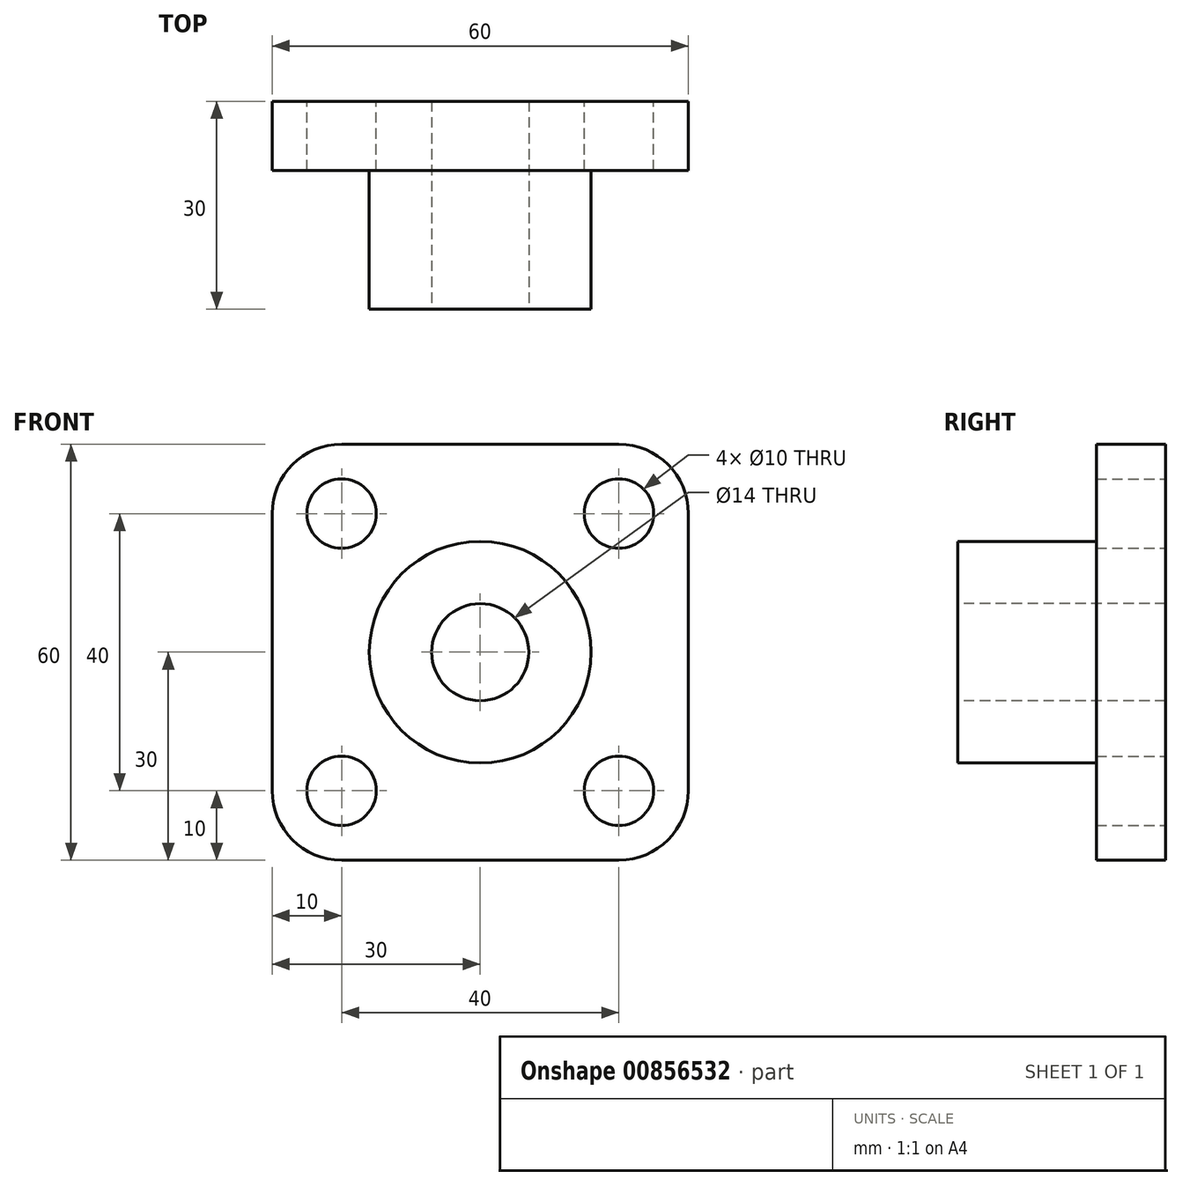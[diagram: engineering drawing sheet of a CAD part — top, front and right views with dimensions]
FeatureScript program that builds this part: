
annotation { "Feature Type Name" : "Feature", "Feature Type Description" : "" }
export const myFeature = defineFeature(function(context is Context, id is Id, definition is map)
    precondition{}
    {
        {
            var Q0;
            Q0=qCreatedBy(makeId("Front.planeOp"),FACE);
            var sketch = newSketch(context, id + "F0", { "sketchPlane" : qUnion([Q0])});
            skCircle(sketch, "E0", {"center": v(0, 0) * mm, "radius": 16 * mm});
            skLineSegment(sketch, "E1", {"start": v(0, 0) * mm, "end": v(-20, 0) * mm});
            skLineSegment(sketch, "E2", {"start": v(0, 0) * mm, "end": v(20, 0) * mm});
            skLineSegment(sketch, "E3", {"start": v(-20, 0) * mm, "end": v(-20, 20) * mm});
            skLineSegment(sketch, "E4", {"start": v(-20, 0) * mm, "end": v(-20, -20) * mm});
            skLineSegment(sketch, "E5", {"start": v(20, 0) * mm, "end": v(20, -20) * mm});
            skLineSegment(sketch, "E6", {"start": v(20, 0) * mm, "end": v(20, 20) * mm});
            skCircle(sketch, "E7", {"center": v(-20, 20) * mm, "radius": 5 * mm});
            skCircle(sketch, "E8", {"center": v(20, 20) * mm, "radius": 5 * mm});
            skCircle(sketch, "E9", {"center": v(-20, -20) * mm, "radius": 5 * mm});
            skCircle(sketch, "E10", {"center": v(20, -20) * mm, "radius": 5 * mm});
            skCircle(sketch, "E11", {"center": v(-20, 20) * mm, "radius": 10 * mm});
            skCircle(sketch, "E12", {"center": v(20, 20) * mm, "radius": 10 * mm});
            skCircle(sketch, "E13", {"center": v(-20, -20) * mm, "radius": 10 * mm});
            skCircle(sketch, "E14", {"center": v(20, -20) * mm, "radius": 10 * mm});
            skLineSegment(sketch, "E15", {"start": v(-20, -30) * mm, "end": v(20, -30) * mm});
            skLineSegment(sketch, "E16", {"start": v(30, 20) * mm, "end": v(30, -20) * mm});
            skLineSegment(sketch, "E17.trimOffspring", {"start": v(-20, 30) * mm, "end": v(20, 30) * mm});
            skLineSegment(sketch, "E18.trimOffspring", {"start": v(-30, 20) * mm, "end": v(-30, -20) * mm});
            skSolve(sketch);
        }
        {
            var Q0;
            {var subQ5=sQuery(id+"F0.wireOp",EDGE,"E17.trimOffspring");Q0=makeQuery(id+"F0.imprint","IMPRINT",FACE,{"disambiguationData":[TD([[makeQuery(id+"F0.imprint","IMPRINT",EDGE,{"derivedFrom":subQ5}),-1.0]])]});}
            var Q1;
            {var subQ13=sQuery(id+"F0.wireOp",EDGE,"E15");Q1=makeQuery(id+"F0.imprint","IMPRINT",FACE,{"disambiguationData":[TD([[makeQuery(id+"F0.imprint","IMPRINT",EDGE,{"derivedFrom":subQ13}),1.0]])]});}
            var Q2;
            {var subQ0=sQuery(id+"F0.wireOp",EDGE,"E16");Q2=makeQuery(id+"F0.imprint","IMPRINT",FACE,{"disambiguationData":[TD([[makeQuery(id+"F0.imprint","IMPRINT",EDGE,{"derivedFrom":subQ0}),-1.0]])]});}
            var Q3;
            Q3=makeQuery(id+"F0.imprint","IMPRINT",FACE,{"disambiguationData":[TD([[makeQuery(id+"F0.imprint","IMPRINT",EDGE,{"derivedFrom":sQuery(id+"F0.wireOp",EDGE,"E8")}),-1.0]])]});
            var Q4;
            Q4=makeQuery(id+"F0.imprint","IMPRINT",FACE,{"disambiguationData":[TD([[makeQuery(id+"F0.imprint","IMPRINT",EDGE,{"derivedFrom":sQuery(id+"F0.wireOp",EDGE,"E7")}),-1.0]])]});
            var Q5;
            {var subQ0=sQuery(id+"F0.wireOp",EDGE,"E18.trimOffspring");Q5=makeQuery(id+"F0.imprint","IMPRINT",FACE,{"disambiguationData":[TD([[makeQuery(id+"F0.imprint","IMPRINT",EDGE,{"derivedFrom":subQ0}),1.0]])]});}
            var Q6;
            Q6=makeQuery(id+"F0.imprint","IMPRINT",FACE,{"disambiguationData":[TD([[makeQuery(id+"F0.imprint","IMPRINT",EDGE,{"derivedFrom":sQuery(id+"F0.wireOp",EDGE,"E9")}),-1.0]])]});
            var Q7;
            Q7=makeQuery(id+"F0.imprint","IMPRINT",FACE,{"disambiguationData":[TD([[makeQuery(id+"F0.imprint","IMPRINT",EDGE,{"derivedFrom":sQuery(id+"F0.wireOp",EDGE,"E10")}),-1.0]])]});
            var Q8;
            {var subQ0=sQuery(id+"F0.wireOp",EDGE,"E1");var subQ1=sQuery(id+"F0.wireOp",EDGE,"E0");var subQ2=makeQuery(id+"F0.imprint","INTERSECT",VERTEX,{"derivedFrom":[subQ1,subQ0]});Q8=makeQuery(id+"F0.imprint","IMPRINT",FACE,{"disambiguationData":[TD([[makeQuery(id+"F0.imprint","IMPRINT",EDGE,{"disambiguationData":[TD([[subQ2,1.0]])],"derivedFrom":subQ1}),1.0]])]});}
            var Q9;
            {var subQ0=sQuery(id+"F0.wireOp",EDGE,"E1");var subQ1=sQuery(id+"F0.wireOp",EDGE,"E0");var subQ2=makeQuery(id+"F0.imprint","INTERSECT",VERTEX,{"derivedFrom":[subQ1,subQ0]});Q9=makeQuery(id+"F0.imprint","IMPRINT",FACE,{"disambiguationData":[TD([[makeQuery(id+"F0.imprint","IMPRINT",EDGE,{"disambiguationData":[TD([[subQ2,-1.0]])],"derivedFrom":subQ1}),1.0]])]});}
            extrude(context, id + "F1", {"entities" : qUnion([Q0, Q1, Q2, Q3, Q4, Q5, Q6, Q7, Q8, Q9]), "depth" : 10 * mm, "offsetDistance" : 25 * mm});
        }
        {
            var Q0;
            Q0=makeQuery(id+"F1.opExtrude","CAP_FACE",FACE,{"disambiguationData":[OSD([sQuery(id+"F0.wireOp",EDGE,"E0"),sQuery(id+"F0.wireOp",EDGE,"E7"),sQuery(id+"F0.wireOp",EDGE,"E8"),sQuery(id+"F0.wireOp",EDGE,"E9"),sQuery(id+"F0.wireOp",EDGE,"E10"),sQuery(id+"F0.wireOp",EDGE,"E11"),sQuery(id+"F0.wireOp",EDGE,"E12"),sQuery(id+"F0.wireOp",EDGE,"E13"),sQuery(id+"F0.wireOp",EDGE,"E14"),sQuery(id+"F0.wireOp",EDGE,"E15"),sQuery(id+"F0.wireOp",EDGE,"E16"),sQuery(id+"F0.wireOp",EDGE,"E17.trimOffspring"),sQuery(id+"F0.wireOp",EDGE,"E18.trimOffspring")])],"isStart":false});
            var sketch = newSketch(context, id + "F2", { "sketchPlane" : qUnion([Q0])});
            skCircle(sketch, "E19", {"center": v(0, 0) * mm, "radius": 16 * mm});
            skSolve(sketch);
        }
        {
            var Q0;
            Q0=makeQuery(id+"F2.imprint","IMPRINT",FACE,{"disambiguationData":[TD([[makeQuery(id+"F2.imprint","IMPRINT",EDGE,{"derivedFrom":sQuery(id+"F2.wireOp",EDGE,"E19")}),1.0]])]});
            extrude(context, id + "F3", {"entities" : qUnion([Q0]), "operationType" : NewBodyOperationType.ADD, "depth" : 20 * mm, "offsetDistance" : 25 * mm});
        }
        {
            var Q0;
            Q0=makeQuery(id+"F3.opExtrude","CAP_FACE",FACE,{"disambiguationData":[OSD([sQuery(id+"F2.wireOp",EDGE,"E19")])],"isStart":false});
            var sketch = newSketch(context, id + "F4", { "sketchPlane" : qUnion([Q0])});
            skPoint(sketch, "E20", {"position": v(0, 0) * mm});
            skSolve(sketch);
        }
        {
            var Q0;
            Q0=sQuery(id+"F4.wireOp",VERTEX,"E20");
            var Q1;
            Q1=makeQuery(id+"F1.opExtrude","SWEPT_BODY",BODY,{"disambiguationData":[OSD([sQuery(id+"F0.wireOp",EDGE,"E7"),sQuery(id+"F0.wireOp",EDGE,"E8"),sQuery(id+"F0.wireOp",EDGE,"E9"),sQuery(id+"F0.wireOp",EDGE,"E10"),sQuery(id+"F0.wireOp",EDGE,"E11"),sQuery(id+"F0.wireOp",EDGE,"E12"),sQuery(id+"F0.wireOp",EDGE,"E13"),sQuery(id+"F0.wireOp",EDGE,"E14"),sQuery(id+"F0.wireOp",EDGE,"E15"),sQuery(id+"F0.wireOp",EDGE,"E16"),sQuery(id+"F0.wireOp",EDGE,"E17.trimOffspring"),sQuery(id+"F0.wireOp",EDGE,"E18.trimOffspring")])]});
            hole(context, id + "F5", {"style" : HoleStyle.SIMPLE, "endStyle" : HoleEndStyle.THROUGH, "standardTappedOrClearance" : lookupTablePath({ "standard" : "ISO", "engagement" : "75%", "pitch" : "2 mm", "size" : "M16", "type" : "Tapped" }), "standardBlindInLast" : lookupTablePath({ "standard" : "ISO", "engagement" : "75%", "pitch" : "2 mm", "size" : "M16", "type" : "Tapped" }), "holeDiameter" : 14 * mm, "majorDiameter" : 16 * mm, "showTappedDepth" : true, "isTappedThrough" : true, "tappedDepth" : 25 * mm, "tapClearance" : 3, "locations" : qUnion([Q0]), "scope" : qUnion([Q1])});
        }
    });
